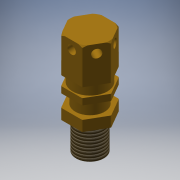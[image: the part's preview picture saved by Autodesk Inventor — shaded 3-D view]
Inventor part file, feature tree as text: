
AUTODESK INVENTOR PART (.ipt)
format: ipt  version: 2017.1 (Build 211199000, 199)  size: 220,672 bytes
history: native  units: mm (DEFAULTED — no unit token found)
features: sketch x9, projected_geometry x9, extrude x8, pattern_circular x1, thread x1, fillet x1, revolve x1
ambient origin geometry x8: Origin, YZ Plane, XZ Plane, XY Plane, X Axis, Y Axis, Z Axis, Center Point
bodies: Solid1 (feature_tree)
feature tree (30):
  extrude  "Extrusion1"  Depth=17.0mm TaperAngle=0.0deg
  extrude  "Extrusion2"  Depth=4.5mm TaperAngle=0.0deg
  extrude  "Extrusion3"  Depth=14.0mm
  extrude  "Extrusion4"  Depth=5.0mm TaperAngle=0.0deg
  extrude  "Extrusion5"  Depth=14.5mm TaperAngle=0.0deg
  extrude  "Extrusion6"  Depth=47.5mm TaperAngle=0.0deg
  extrude  "Extrusion7"  Depth=4.0mm
  extrude  "Extrusion8"  Depth=30.0mm TaperAngle=360.0deg
  pattern_circular  "Circular Pattern1"  Angle=45.0deg  [1 undecoded]
  thread  "Thread1"  [1 undecoded]
  fillet  "Fillet1"  [1 undecoded]
  revolve  "Revolution2"  [1 undecoded]
  sketch  "Sketch1"  dims[d0=17.5mm d1=17.0mm d2=0.0mm]
  sketch  "Sketch2"  dims[d3=16.5mm d4=4.5mm d5=0.0mm]
  projected_geometry  "Projected Loop1"
  sketch  "Sketch3"  dims[d6=3.0mm d7=0.0mm d8=14.0mm]
  projected_geometry  "Projected Loop2"
  sketch  "Sketch4"  dims[d9=6.0mm d10=0.0mm d11=5.0mm d12=0.0mm]
  projected_geometry  "Projected Loop3"
  sketch  "Sketch5"  dims[d13=13.25mm d14=14.5mm d15=0.0mm]
  projected_geometry  "Projected Loop4"
  sketch  "Sketch6"  dims[d16=5.0mm d17=47.5mm d18=0.0mm]
  projected_geometry  "Projected Loop5"
  sketch  "Sketch7"  dims[d19=4.0mm d20=4.0mm]
  projected_geometry  "Projected Loop6"
  sketch  "Sketch8"  dims[d21=40.25mm d22=0.0mm d23=30.0mm d25=360.0deg]
  projected_geometry  "Projected Loop7"
  sketch  "Sketch10"  dims[d26=10.0mm d27=0.0mm d28=0.5mm d32=45.0deg d33=1.0mm d34=90.0deg]
  projected_geometry  "Projected Loop8"
  projected_geometry  "Projected Loop9"
note: 4 required parameter values undecoded (feature->parameter linkage not recoverable at this tier; creation-order binding heuristic only, values carry confidence <= 0.55)
